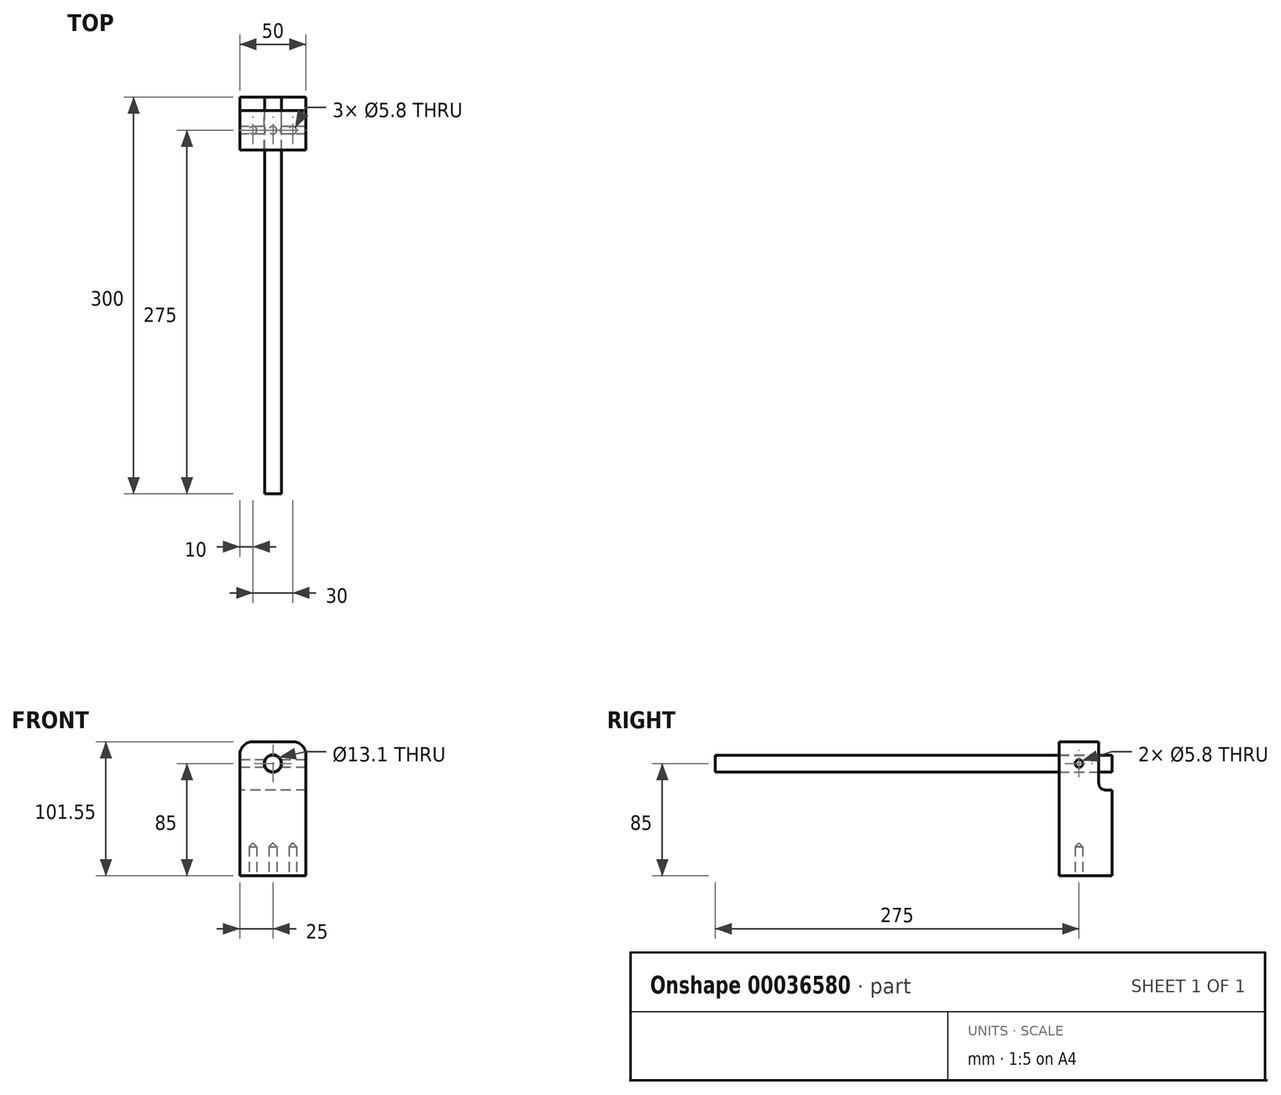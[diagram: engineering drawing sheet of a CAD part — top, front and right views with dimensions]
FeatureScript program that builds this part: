
annotation { "Feature Type Name" : "Feature", "Feature Type Description" : "" }
export const myFeature = defineFeature(function(context is Context, id is Id, definition is map)
    precondition{}
    {
        {
            var Q0;
            Q0=qCreatedBy(makeId("Front.planeOp"),FACE);
            var sketch = newSketch(context, id + "F0", { "sketchPlane" : qUnion([Q0])});
            skLineSegment(sketch, "E0.bottom", {"start": v(0, 0) * mm, "end": v(50, 0) * mm});
            skLineSegment(sketch, "E0.top", {"start": v(0, 101.55) * mm, "end": v(50, 101.55) * mm});
            skLineSegment(sketch, "E0.left", {"start": v(0, 0) * mm, "end": v(0, 101.55) * mm});
            skLineSegment(sketch, "E0.right", {"start": v(50, 0) * mm, "end": v(50, 101.55) * mm});
            skCircle(sketch, "E1", {"center": v(25, 85) * mm, "radius": 6.55 * mm});
            skLineSegment(sketch, "E2", {"start": v(25, 101.55) * mm, "end": v(25, 0) * mm, "construction": true});
            skCircle(sketch, "E3", {"center": v(25, 85) * mm, "radius": 6.35 * mm});
            skSolve(sketch);
        }
        {
            var Q0;
            Q0=makeQuery(id+"F0.imprint","IMPRINT",FACE,{"disambiguationData":[TD([[makeQuery(id+"F0.imprint","IMPRINT",EDGE,{"derivedFrom":sQuery(id+"F0.wireOp",EDGE,"E0.bottom")}),1.0]])]});
            extrude(context, id + "F1", {"entities" : qUnion([Q0]), "depth" : 40 * mm});
        }
        {
            var Q0;
            Q0=sQuery(id+"F0.wireOp",VERTEX,"E1.center");
            var Q1;
            Q1=makeQuery(id+"F1.opExtrude","SWEPT_FACE",FACE,{"disambiguationData":[OSD([sQuery(id+"F0.wireOp",EDGE,"E0.top")])]});
            cPlane(context, id + "F2", {"entities" : qUnion([Q0, Q1]), "cplaneType" : CPlaneType.PLANE_POINT, "offset" : 25 * mm, "width" : 150 * mm, "height" : 150 * mm});
        }
        {
            var Q0;
            Q0=makeQuery(id+"F1.opExtrude","SWEPT_FACE",FACE,{"disambiguationData":[OSD([sQuery(id+"F0.wireOp",EDGE,"E0.left")])]});
            var sketch = newSketch(context, id + "F3", { "sketchPlane" : qUnion([Q0])});
            skLineSegment(sketch, "E4", {"start": v(25, 100.83) * mm, "end": v(25, 0) * mm, "construction": true});
            skCircle(sketch, "E5", {"center": v(25, 85) * mm, "radius": 2.9 * mm});
            skSolve(sketch);
        }
        {
            var Q0;
            Q0=makeQuery(id+"F3.imprint","IMPRINT",FACE,{"disambiguationData":[TD([[makeQuery(id+"F3.imprint","IMPRINT",EDGE,{"derivedFrom":sQuery(id+"F3.wireOp",EDGE,"E5")}),1.0]])]});
            extrude(context, id + "F4", {"entities" : qUnion([Q0]), "operationType" : NewBodyOperationType.REMOVE, "endBound" : BoundingType.THROUGH_ALL, "oppositeDirection" : true, "depth" : 25 * mm});
        }
        {
            var Q0;
            Q0=makeQuery(id+"F1.opExtrude","SWEPT_FACE",FACE,{"disambiguationData":[OSD([sQuery(id+"F0.wireOp",EDGE,"E0.bottom")])]});
            var sketch = newSketch(context, id + "F5", { "sketchPlane" : qUnion([Q0])});
            skCircle(sketch, "E6", {"center": v(40, 25) * mm, "radius": 2.9 * mm});
            skLineSegment(sketch, "E7", {"start": v(-0.31, 25) * mm, "end": v(48.9, 25) * mm, "construction": true});
            skCircle(sketch, "E8.1.0.0", {"center": v(25, 25) * mm, "radius": 2.9 * mm});
            skCircle(sketch, "E8.2.0.0", {"center": v(10, 25) * mm, "radius": 2.9 * mm});
            skLineSegment(sketch, "E8.direction1", {"start": v(40, 25) * mm, "end": v(25, 25) * mm, "construction": true});
            skSolve(sketch);
        }
        {
            var Q0;
            Q0=makeQuery(id+"F5.imprint","IMPRINT",FACE,{"disambiguationData":[TD([[makeQuery(id+"F5.imprint","IMPRINT",EDGE,{"derivedFrom":sQuery(id+"F5.wireOp",EDGE,"E8.2.0.0")}),1.0]])]});
            var Q1;
            Q1=makeQuery(id+"F5.imprint","IMPRINT",FACE,{"disambiguationData":[TD([[makeQuery(id+"F5.imprint","IMPRINT",EDGE,{"derivedFrom":sQuery(id+"F5.wireOp",EDGE,"E8.1.0.0")}),1.0]])]});
            var Q2;
            Q2=makeQuery(id+"F5.imprint","IMPRINT",FACE,{"disambiguationData":[TD([[makeQuery(id+"F5.imprint","IMPRINT",EDGE,{"derivedFrom":sQuery(id+"F5.wireOp",EDGE,"E6")}),1.0]])]});
            extrude(context, id + "F6", {"entities" : qUnion([Q0, Q1, Q2]), "operationType" : NewBodyOperationType.REMOVE, "oppositeDirection" : true, "depth" : 25 * mm});
        }
        {
            var Q0;
            Q0=makeQuery(id+"F6.boolean.opBoolean","COPY",EDGE,{"derivedFrom":makeQuery(id+"F6.opExtrude","CAP_EDGE",EDGE,{"disambiguationData":[OSD([sQuery(id+"F5.wireOp",EDGE,"E8.1.0.0")])],"isStart":false})});
            var Q1;
            Q1=makeQuery(id+"F6.boolean.opBoolean","COPY",EDGE,{"derivedFrom":makeQuery(id+"F6.opExtrude","CAP_EDGE",EDGE,{"disambiguationData":[OSD([sQuery(id+"F5.wireOp",EDGE,"E8.2.0.0")])],"isStart":false})});
            var Q2;
            Q2=makeQuery(id+"F6.boolean.opBoolean","COPY",EDGE,{"derivedFrom":makeQuery(id+"F6.opExtrude","CAP_EDGE",EDGE,{"disambiguationData":[OSD([sQuery(id+"F5.wireOp",EDGE,"E6")])],"isStart":false})});
            chamfer(context, id + "F7", {"entities" : qUnion([Q0, Q1, Q2]), "width" : 2.9 * mm, "tangentPropagation" : true});
        }
        {
            var Q0;
            Q0=makeQuery(id+"F1.opExtrude","SWEPT_EDGE",EDGE,{"disambiguationData":[OSD([sQuery(id+"F0.wireOp",EDGE,"E0.top"),sQuery(id+"F0.wireOp",EDGE,"E0.right")])]});
            var Q1;
            Q1=makeQuery(id+"F1.opExtrude","SWEPT_EDGE",EDGE,{"disambiguationData":[OSD([sQuery(id+"F0.wireOp",EDGE,"E0.top"),sQuery(id+"F0.wireOp",EDGE,"E0.left")])]});
            fillet(context, id + "F8", {"entities" : qUnion([Q0, Q1]), "radius" : 10 * mm, "tangentPropagation" : true, "allowEdgeOverflow" : false});
        }
        {
            var Q0;
            Q0=makeQuery(id+"F0.imprint","IMPRINT",FACE,{"disambiguationData":[TD([[makeQuery(id+"F0.imprint","IMPRINT",EDGE,{"derivedFrom":sQuery(id+"F0.wireOp",EDGE,"E0.bottom")}),1.0]])]});
            var sketch = newSketch(context, id + "F9", { "sketchPlane" : qUnion([Q0])});
            skLineSegment(sketch, "E9", {"start": v(50, 65) * mm, "end": v(0, 65) * mm});
            skSolve(sketch);
        }
        {
            var Q0;
            {var subQ2=sQuery(id+"F9.wireOp",EDGE,"E9");Q0=makeQuery(id+"F9.imprint","IMPRINT",FACE,{"disambiguationData":[TD([[makeQuery(id+"F9.imprint","IMPRINT",EDGE,{"derivedFrom":subQ2}),-1.0]])]});}
            extrude(context, id + "F10", {"entities" : qUnion([Q0]), "operationType" : NewBodyOperationType.REMOVE, "depth" : 10 * mm});
        }
        {
            var Q0;
            Q0=makeQuery(id+"F10.boolean.opBoolean","COPY",EDGE,{"derivedFrom":makeQuery(id+"F10.opExtrude","CAP_EDGE",EDGE,{"disambiguationData":[OSD([sQuery(id+"F9.wireOp",EDGE,"E9")])],"isStart":false})});
            var Q1;
            Q1=makeQuery(id+"F10.boolean.opBoolean","COPY",EDGE,{"derivedFrom":makeQuery(id+"F10.opExtrude","CAP_EDGE",EDGE,{"disambiguationData":[OSD([sQuery(id+"F9.wireOp",EDGE,"E9")])],"isStart":true})});
            fillet(context, id + "F11", {"entities" : qUnion([Q0, Q1]), "radius" : 5 * mm, "tangentPropagation" : true, "allowEdgeOverflow" : false});
        }
        {
            var Q0;
            Q0=makeQuery(id+"F0.imprint","IMPRINT",FACE,{"disambiguationData":[TD([[makeQuery(id+"F0.imprint","IMPRINT",EDGE,{"derivedFrom":sQuery(id+"F0.wireOp",EDGE,"E3")}),1.0]])]});
            extrude(context, id + "F12", {"entities" : qUnion([Q0]), "depth" : 300 * mm});
        }
    });
